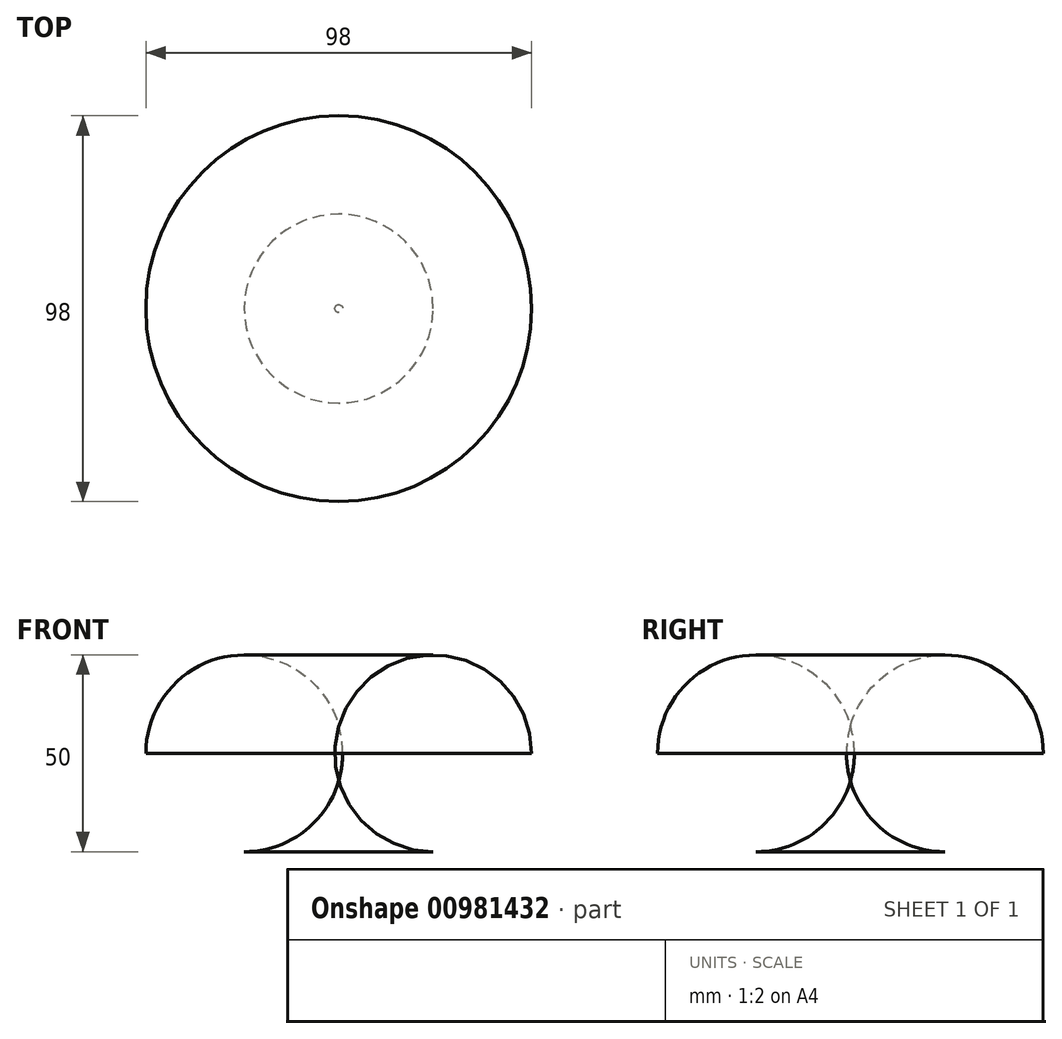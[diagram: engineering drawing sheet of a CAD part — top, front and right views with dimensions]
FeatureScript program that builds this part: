
annotation { "Feature Type Name" : "Feature", "Feature Type Description" : "" }
export const myFeature = defineFeature(function(context is Context, id is Id, definition is map)
    precondition{}
    {
        {
            var Q0;
            Q0=qCreatedBy(makeId("Front.planeOp"),FACE);
            var sketch = newSketch(context, id + "F0", { "sketchPlane" : qUnion([Q0])});
            skLineSegment(sketch, "E0", {"start": v(0, 0) * mm, "end": v(24, 0) * mm});
            skArc(sketch, "E1", {"start": v(24, 0) * mm, "mid": v(41.68, 7.32) * mm, "end": v(49, 25) * mm});
            skLineSegment(sketch, "E2", {"start": v(24, 0) * mm, "end": v(24, 0) * mm});
            skLineSegment(sketch, "E3", {"start": v(0, 0) * mm, "end": v(0, 25) * mm});
            skSolve(sketch);
        }
        {
            var Q0;
            Q0=sQuery(id+"F0.wireOp",EDGE,"E1");
            var Q1;
            Q1=sQuery(id+"F0.wireOp",EDGE,"E3");
            revolve(context, id + "F1", {"bodyType" : ToolBodyType.SURFACE, "surfaceOperationType" : NewSurfaceOperationType.NEW, "surfaceEntities" : qUnion([Q0]), "axis" : qUnion([Q1]), "revolveType" : RevolveType.FULL});
        }
    });
